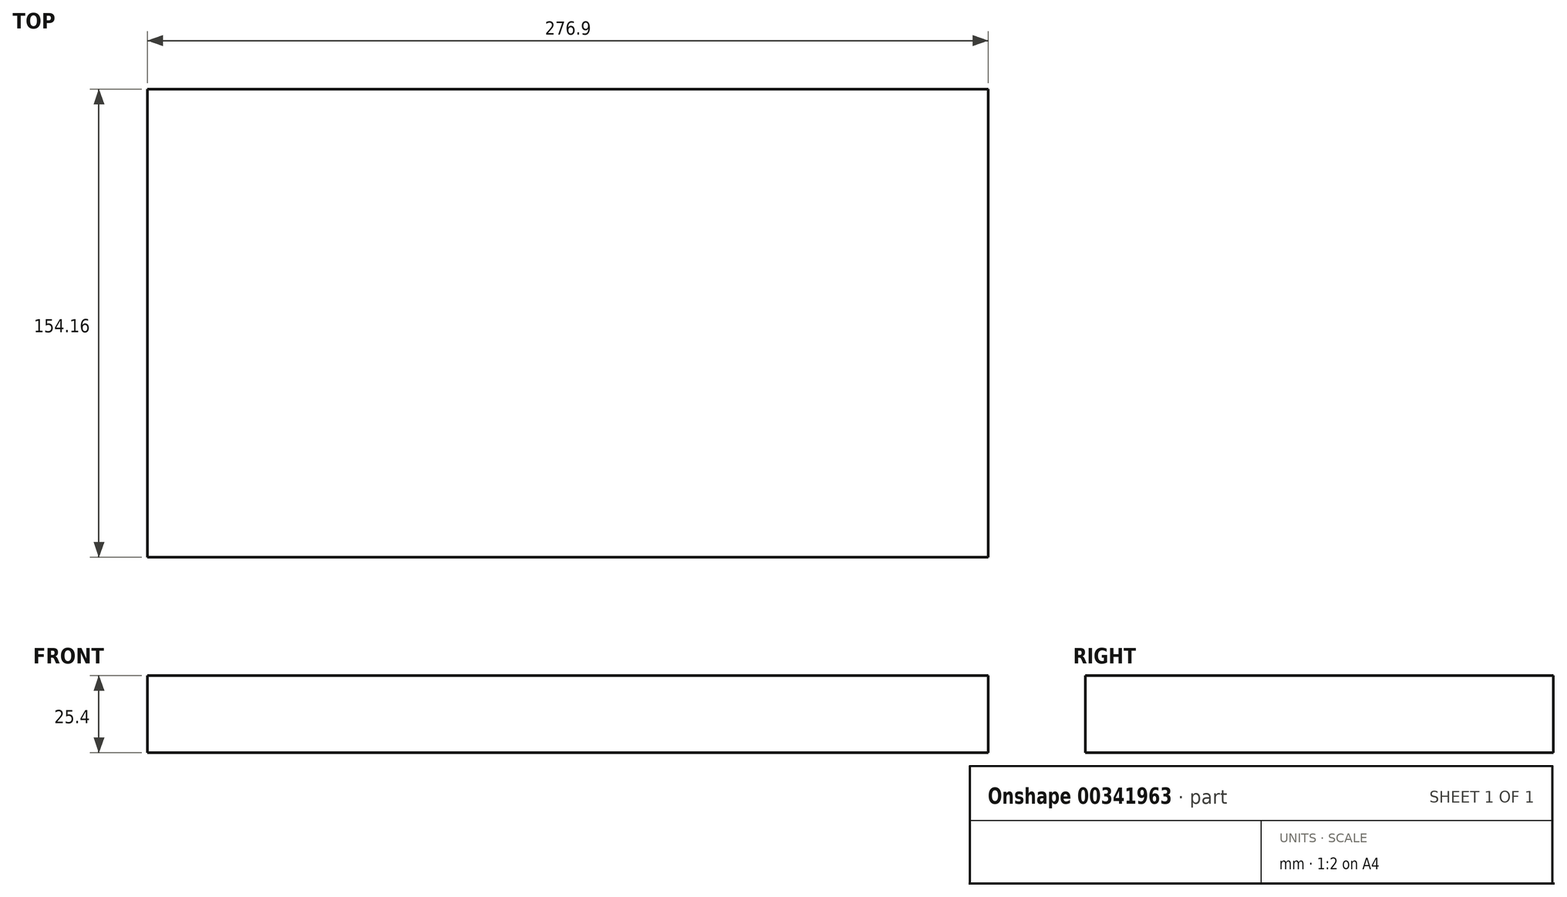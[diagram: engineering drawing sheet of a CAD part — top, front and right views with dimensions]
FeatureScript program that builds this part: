
annotation { "Feature Type Name" : "Feature", "Feature Type Description" : "" }
export const myFeature = defineFeature(function(context is Context, id is Id, definition is map)
    precondition{}
    {
        {
            var Q0;
            Q0=qCreatedBy(makeId("Top.planeOp"),FACE);
            var sketch = newSketch(context, id + "F0", { "sketchPlane" : qUnion([Q0])});
            skLineSegment(sketch, "E0.bottom", {"start": v(-136.58, 72.5) * mm, "end": v(140.32, 72.5) * mm});
            skLineSegment(sketch, "E0.top", {"start": v(-136.58, -81.66) * mm, "end": v(140.32, -81.66) * mm});
            skLineSegment(sketch, "E0.left", {"start": v(-136.58, 72.5) * mm, "end": v(-136.58, -81.66) * mm});
            skLineSegment(sketch, "E0.right", {"start": v(140.32, 72.5) * mm, "end": v(140.32, -81.66) * mm});
            skSolve(sketch);
        }
        {
            var Q0;
            Q0 = qSketchRegion(id + "F0", true);
            extrude(context, id + "F1", {"entities" : qUnion([Q0]), "depth" : 12.7 * mm, "hasSecondDirection" : true, "secondDirectionOppositeDirection" : true, "secondDirectionDepth" : 12.7 * mm});
        }
    });
